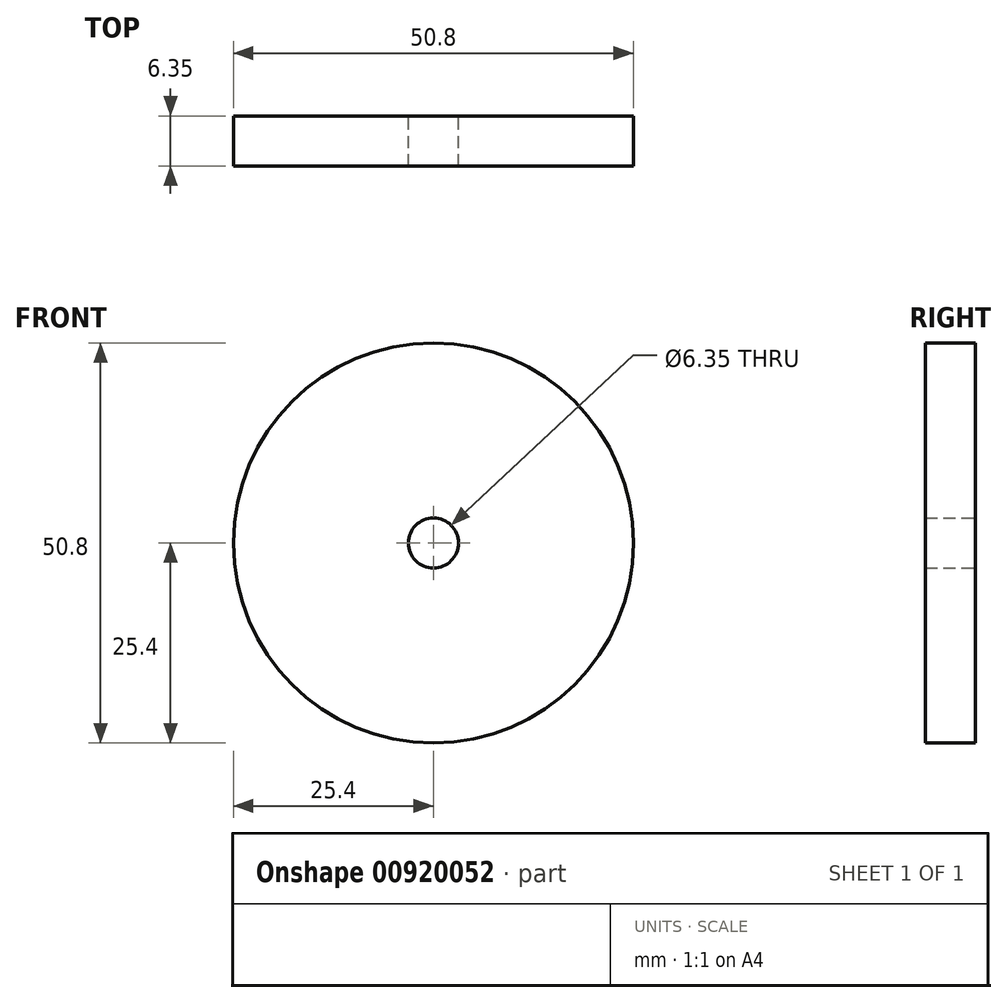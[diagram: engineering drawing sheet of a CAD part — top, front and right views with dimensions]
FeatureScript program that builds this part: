
annotation { "Feature Type Name" : "Feature", "Feature Type Description" : "" }
export const myFeature = defineFeature(function(context is Context, id is Id, definition is map)
    precondition{}
    {
        {
            var Q0;
            Q0=qCreatedBy(makeId("Front.planeOp"),FACE);
            var sketch = newSketch(context, id + "F0", { "sketchPlane" : qUnion([Q0])});
            skCircle(sketch, "E0", {"center": v(0, 0) * mm, "radius": 25.4 * mm});
            skCircle(sketch, "E1", {"center": v(0, 0) * mm, "radius": 3.17 * mm});
            skSolve(sketch);
        }
        {
            var Q0;
            Q0=makeQuery(id+"F0.imprint","IMPRINT",FACE,{"disambiguationData":[TD([[makeQuery(id+"F0.imprint","IMPRINT",EDGE,{"derivedFrom":sQuery(id+"F0.wireOp",EDGE,"E0")}),1.0]])]});
            extrude(context, id + "F1", {"entities" : qUnion([Q0]), "depth" : 6.35 * mm, "offsetDistance" : 25.4 * mm});
        }
    });
